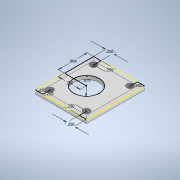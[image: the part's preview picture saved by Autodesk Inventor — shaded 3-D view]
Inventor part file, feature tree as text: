
AUTODESK INVENTOR PART (.ipt)
format: ipt  version: 2020 (Build 240168000, 168)  size: 143,360 bytes
history: native  units: in
note: dims shown in document units (in); Inventor stores cm internally (conversion verified against a paired STEP export)
features: extrude x2, hole x1, fillet x1, sketch x1
ambient origin geometry x8: Origin, YZ Plane, XZ Plane, XY Plane, X Axis, Y Axis, Z Axis, Center Point
bodies: Solid1 (feature_tree)
feature tree (5):
  extrude  "Extrusion1"  Depth=0.125in
  hole  "Hole1"  [1 undecoded]
  extrude  "Extrusion2"  Depth=0.125in
  fillet  "Fillet1"  Radius=0.25in
  sketch  "Sketch1"  dims[d0=1.75in d1=1.988in d2=0.125in d3=0.0in d4=0.25in d5=0.25in d6=0.25in d7=0.25in d8=0.129in d9=0.75in d10=0.219in d11=0.0625in d12=0.5635in d13=0.5in d14=0.8108in d15=0.994in d16=0.75in d17=0.875in d18=0.125in d19=0.0in d20=0.125in d21=0.25in d22=0.25in d23=0.25in]
note: 1 required parameter value undecoded (feature->parameter linkage not recoverable at this tier; creation-order binding heuristic only, values carry confidence <= 0.55)
